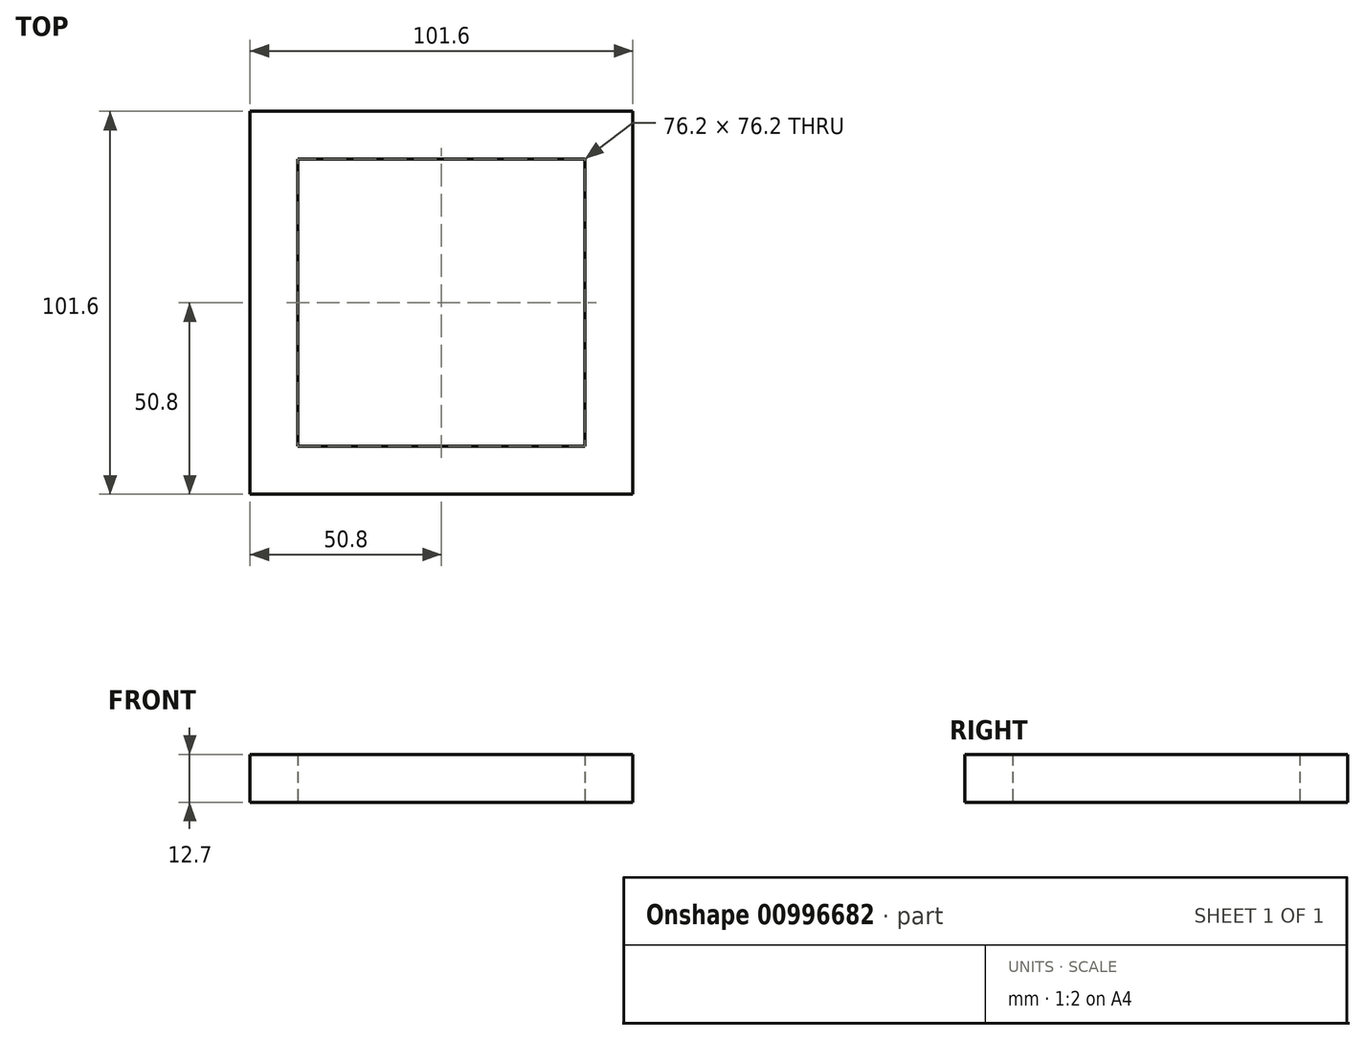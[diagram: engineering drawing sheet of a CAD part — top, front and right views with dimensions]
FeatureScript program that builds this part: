
annotation { "Feature Type Name" : "Feature", "Feature Type Description" : "" }
export const myFeature = defineFeature(function(context is Context, id is Id, definition is map)
    precondition{}
    {
        {
            var Q0;
            Q0=qCreatedBy(makeId("Top.planeOp"),FACE);
            var sketch = newSketch(context, id + "F0", { "sketchPlane" : qUnion([Q0])});
            skLineSegment(sketch, "E0.bottom", {"start": v(-38.1, 38.1) * mm, "end": v(38.1, 38.1) * mm});
            skLineSegment(sketch, "E0.top", {"start": v(-38.1, -38.1) * mm, "end": v(38.1, -38.1) * mm});
            skLineSegment(sketch, "E0.left", {"start": v(-38.1, 38.1) * mm, "end": v(-38.1, -38.1) * mm});
            skLineSegment(sketch, "E0.right", {"start": v(38.1, 38.1) * mm, "end": v(38.1, -38.1) * mm});
            skLineSegment(sketch, "E1.bottom", {"start": v(-50.8, 50.8) * mm, "end": v(50.8, 50.8) * mm});
            skLineSegment(sketch, "E1.top", {"start": v(-50.8, -50.8) * mm, "end": v(50.8, -50.8) * mm});
            skLineSegment(sketch, "E1.left", {"start": v(-50.8, 50.8) * mm, "end": v(-50.8, -50.8) * mm});
            skLineSegment(sketch, "E1.right", {"start": v(50.8, 50.8) * mm, "end": v(50.8, -50.8) * mm});
            skLineSegment(sketch, "E2", {"start": v(-38.1, 38.1) * mm, "end": v(38.1, -38.1) * mm, "construction": true});
            skLineSegment(sketch, "E3", {"start": v(-50.8, 50.8) * mm, "end": v(50.8, -50.8) * mm, "construction": true});
            skSolve(sketch);
        }
        {
            var Q0;
            Q0 = qSketchRegion(id + "F0", true);
            extrude(context, id + "F1", {"entities" : qUnion([Q0]), "depth" : 12.7 * mm, "offsetDistance" : 25.4 * mm});
        }
    });
